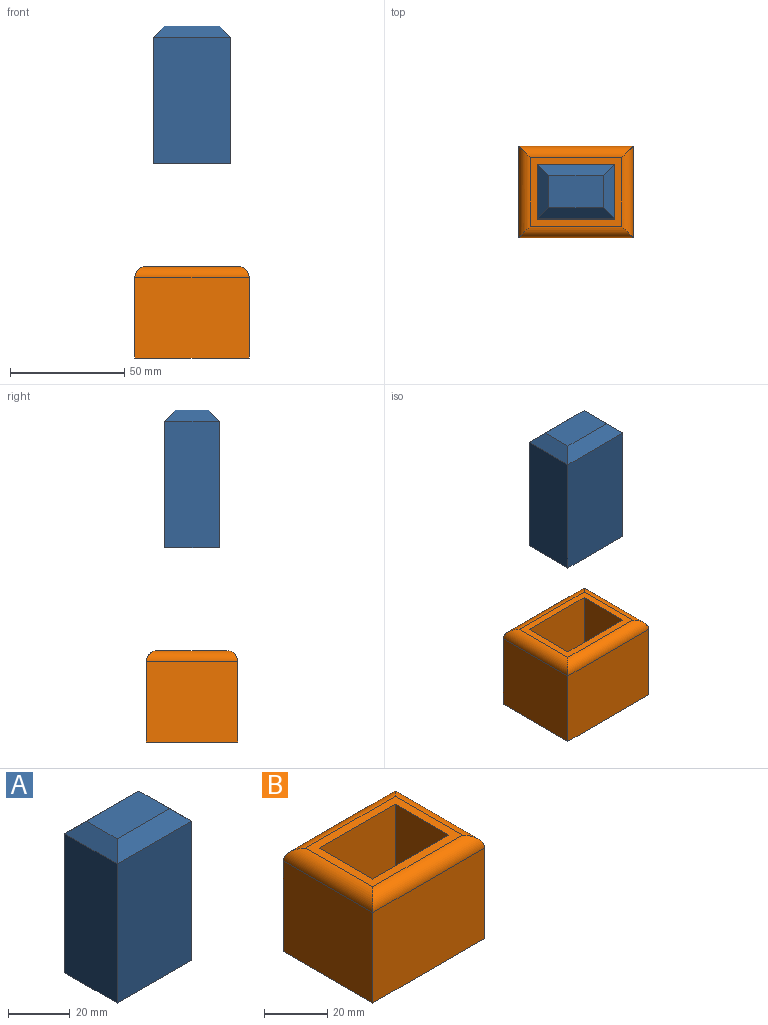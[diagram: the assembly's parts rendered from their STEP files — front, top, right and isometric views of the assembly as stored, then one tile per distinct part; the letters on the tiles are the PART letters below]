
ASSEMBLY  parts=2 mates=1
PART A: 10 faces, bbox 34x24x60.3 mm
  f0: plane 55.3x24mm, normal (-1,0,0), area 1327.2mm2, adj f1,f3,f5,f6
  f1: plane 55.3x34mm, normal (0,-1,0), area 1880.2mm2, adj f0,f2,f5,f7
  f2: plane 55.3x24mm, normal (1,0,0), area 1327.2mm2, adj f1,f3,f5,f9
  f3: plane 55.3x34mm, normal (0,1,0), area 1880.2mm2, adj f0,f2,f5,f8
  f4: plane 24x14mm, normal (0,0,1), area 336mm2, adj f6,f7,f8,f9
  f5: plane 34x24mm, normal (0,0,-1), area 816mm2, adj f0,f1,f2,f3
  f6: plane 24x5mm, normal (-0.71,0,0.71), area 134.4mm2, adj f0,f4,f7,f8
  f7: plane 34x5mm, normal (0,-0.71,0.71), area 205.1mm2, adj f1,f4,f6,f9
  f8: plane 34x5mm, normal (0,0.71,0.71), area 205.1mm2, adj f3,f4,f6,f9
  f9: plane 24x5mm, normal (0.71,0,0.71), area 134.4mm2, adj f2,f4,f7,f8
PART B: 15 faces, bbox 50x40x40 mm
  f0: plane 40x35mm, normal (-1,0,0), area 1400mm2, adj f1,f4,f5,f11
  f1: plane 50x40mm, normal (0,0,-1), area 2000mm2, adj f0,f2,f4,f5
  f2: plane 40x35mm, normal (1,0,0), area 1400mm2, adj f1,f4,f5,f14
  f3: plane 40x30mm, normal (0,0,1), area 384mm2, adj f6,f7,f8,f9,f11,f12,f13,f14
  f4: plane 50x35mm, normal (0,-1,0), area 1750mm2, adj f0,f1,f2,f12
  f5: plane 50x35mm, normal (0,1,0), area 1750mm2, adj f0,f1,f2,f13
  f6: plane 34.4x34mm, normal (0,-1,0), area 1169.6mm2, adj f3,f7,f9,f10
  f7: plane 34.4x24mm, normal (1,0,0), area 825.6mm2, adj f3,f6,f8,f10
  f8: plane 34.4x34mm, normal (0,1,0), area 1169.6mm2, adj f3,f7,f9,f10
  f9: plane 34.4x24mm, normal (-1,0,0), area 825.6mm2, adj f3,f6,f8,f10
  f10: plane 34x24mm, normal (0,0,1), area 816mm2, adj f6,f7,f8,f9
  f11: cylinder r=5mm len=40mm, axis (0,1,0), area 285.6mm2, adj f0,f3,f12,f13
  f12: cylinder r=5mm len=50mm, axis (1,0,0), area 364.2mm2, adj f3,f4,f11,f14
  f13: cylinder r=5mm len=50mm, axis (-1,0,0), area 364.2mm2, adj f3,f5,f11,f14
  f14: cylinder r=5mm len=40mm, axis (0,-1,0), area 285.6mm2, adj f2,f3,f12,f13
PLACE A t=(-60.19,2.25,61.92)mm
PLACE B t=(-68.19,35.32,-22.92)mm fixed
MATE slider B.f10 <-> A.f5  axis (0,0,1) through (-43.19,15.32,-17.32)mm
